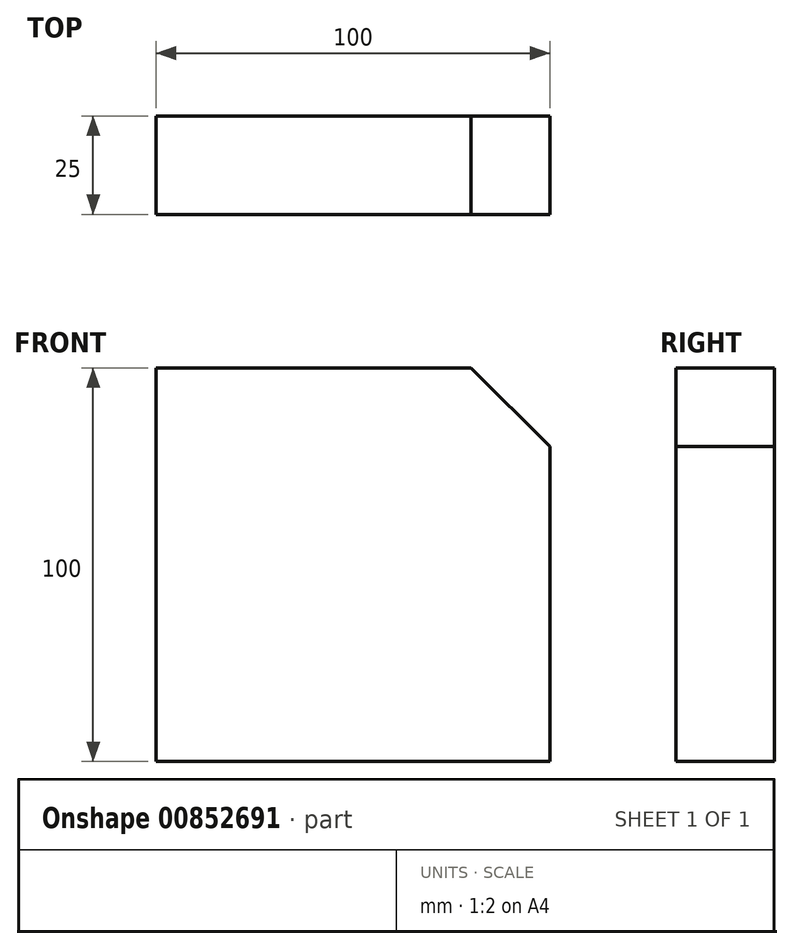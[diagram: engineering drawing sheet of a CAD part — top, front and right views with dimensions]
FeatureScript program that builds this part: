
annotation { "Feature Type Name" : "Feature", "Feature Type Description" : "" }
export const myFeature = defineFeature(function(context is Context, id is Id, definition is map)
    precondition{}
    {
        {
            var Q0;
            Q0=qCreatedBy(makeId("Front.planeOp"),FACE);
            var sketch = newSketch(context, id + "F0", { "sketchPlane" : qUnion([Q0])});
            skLineSegment(sketch, "E0.bottom", {"start": v(-46.35, 50.09) * mm, "end": v(53.65, 50.09) * mm});
            skLineSegment(sketch, "E0.top", {"start": v(-46.35, -49.91) * mm, "end": v(53.65, -49.91) * mm});
            skLineSegment(sketch, "E0.left", {"start": v(-46.35, 50.09) * mm, "end": v(-46.35, -49.91) * mm});
            skLineSegment(sketch, "E0.right", {"start": v(53.65, 50.09) * mm, "end": v(53.65, -49.91) * mm});
            skSolve(sketch);
        }
        {
            var Q0;
            Q0 = qSketchRegion(id + "F0", true);
            extrude(context, id + "F1", {"entities" : qUnion([Q0]), "depth" : 25 * mm, "offsetDistance" : 25 * mm});
        }
        {
            var Q0;
            Q0=makeQuery(id+"F1.opExtrude","SWEPT_EDGE",EDGE,{"disambiguationData":[OSD([sQuery(id+"F0.wireOp",EDGE,"E0.bottom"),sQuery(id+"F0.wireOp",EDGE,"E0.right")])]});
            chamfer(context, id + "F2", {"entities" : qUnion([Q0]), "width" : 20 * mm, "tangentPropagation" : true});
        }
    });
